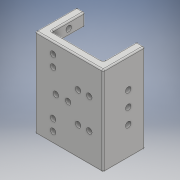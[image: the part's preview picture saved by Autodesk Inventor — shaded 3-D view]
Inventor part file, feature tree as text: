
AUTODESK INVENTOR PART (.ipt)
format: ipt  version: 2018 (Build 220112000, 112)  size: 244,224 bytes
history: native  units: mm
features: extrude x5, sketch x3, fillet x1
ambient origin geometry x8: Origin, YZ Plane, XZ Plane, XY Plane, X Axis, Y Axis, Z Axis, Center Point
bodies: Solid1 (feature_tree)
feature tree (9):
  sketch  "Sketch1"  dims[d0=24.5mm d1=32.0mm]
  extrude  "Extrusion1"  Depth=32.0mm
  extrude  "Extrusion2"  Depth=4.7mm
  extrude  "Extrusion3"  Depth=3.0mm
  sketch  "Sketch3"  dims[d4=4.7mm d5=3.0mm d6=2.0mm d7=2.0mm d8=2.0mm d9=2.0mm d10=2.0mm d11=2.0mm d12=2.0mm d13=2.0mm d14=2.0mm d15=2.0mm d16=4.0mm d17=4.0mm d18=4.0mm d19=4.0mm d20=18.0mm d21=18.0mm d22=18.0mm d23=18.0mm d24=5.0mm d25=4.0mm d26=5.0mm d27=4.0mm d28=10.6mm d29=10.6mm d30=10.6mm d31=10.6mm d32=16.0mm d33=16.0mm d34=4.4mm d35=12.6mm d36=3.0mm d37=3.0mm d38=0.0mm d39=15.0mm d40=0.0mm d41=2.0mm d42=2.0mm d43=5.9mm d44=5.9mm d45=2.3mm d46=2.3mm d47=3.0mm d48=0.0mm d51=2.0mm d52=2.0mm d53=6.0mm d54=10.6mm d55=6.0mm d56=10.6mm d57=3.0mm d58=0.0mm d59=0.5mm d60=2.0mm d61=6.0mm d62=16.0mm d63=3.0mm d64=0.0mm]
  extrude  "Extrusion4"  Depth=3.0mm
  fillet  "Fillet3"  Radius=2.0mm
  extrude  "Extrusion5"  Depth=3.0mm
  sketch  "Sketch2"  dims[d2=3.0mm d3=4.7mm]
